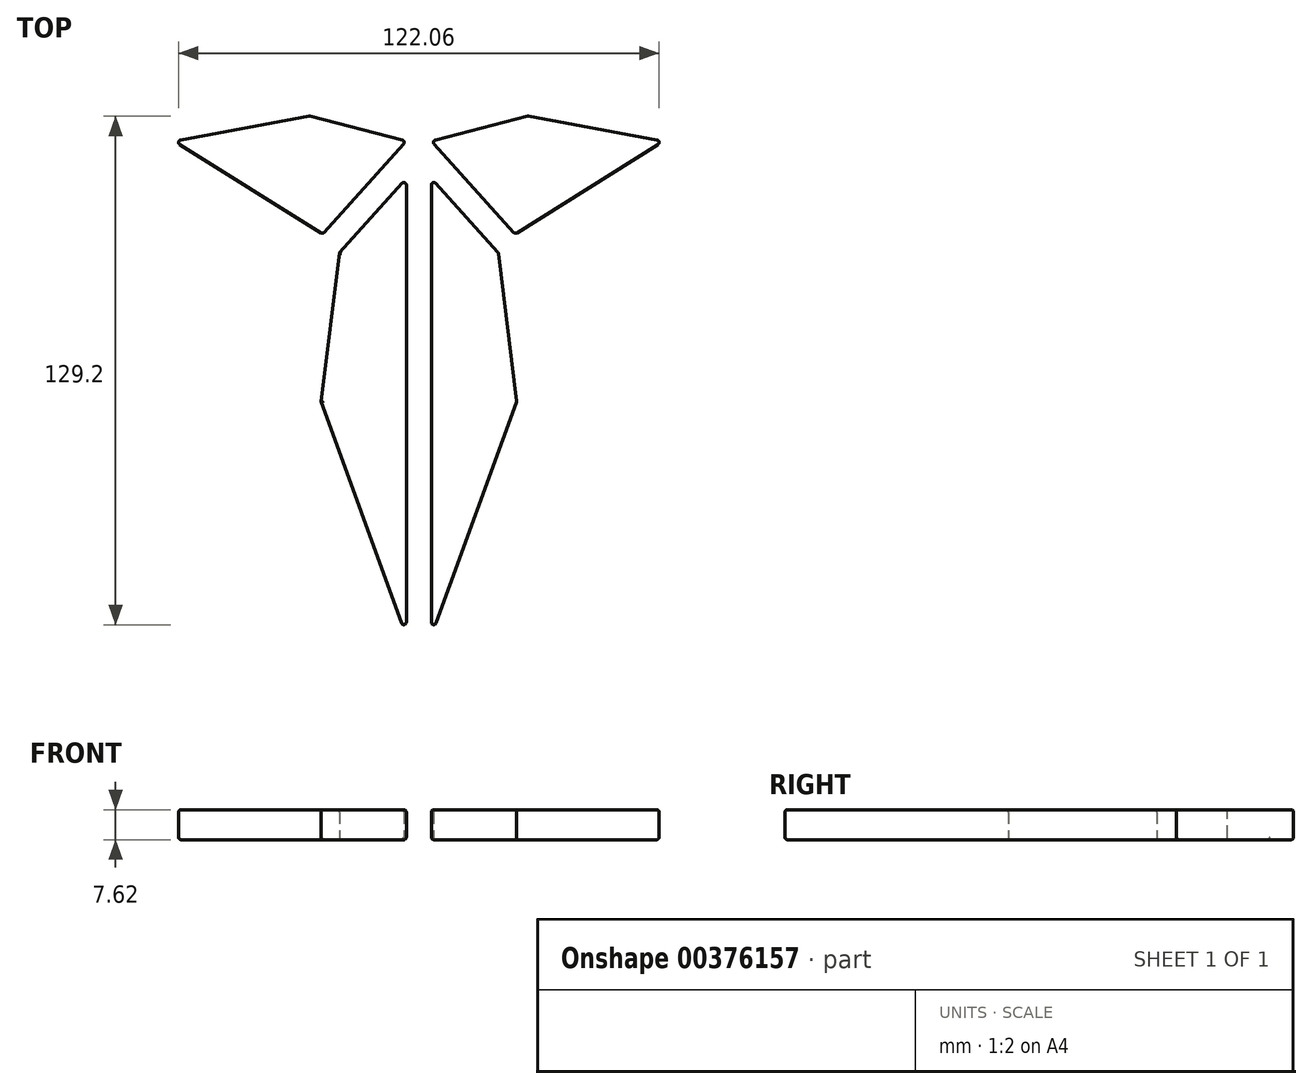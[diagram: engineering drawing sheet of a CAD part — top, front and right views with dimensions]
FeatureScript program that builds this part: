
annotation { "Feature Type Name" : "Feature", "Feature Type Description" : "" }
export const myFeature = defineFeature(function(context is Context, id is Id, definition is map)
    precondition{}
    {
        {
            var Q0;
            Q0=qCreatedBy(makeId("Top.planeOp"),FACE);
            var sketch = newSketch(context, id + "F0", { "sketchPlane" : qUnion([Q0])});
            skLineSegment(sketch, "E0", {"start": v(-3.18, 88.64) * mm, "end": v(-24.44, 65.06) * mm});
            skLineSegment(sketch, "E1", {"start": v(-24.44, 65.06) * mm, "end": v(-62.12, 88.64) * mm});
            skLineSegment(sketch, "E2", {"start": v(-62.12, 88.64) * mm, "end": v(-27.77, 94.98) * mm});
            skLineSegment(sketch, "E3", {"start": v(-27.77, 94.98) * mm, "end": v(-3.18, 88.64) * mm});
            skLineSegment(sketch, "E4", {"start": v(-3.18, 79.16) * mm, "end": v(-20.18, 60.3) * mm});
            skLineSegment(sketch, "E5", {"start": v(-20.18, 60.3) * mm, "end": v(-24.85, 22.48) * mm});
            skLineSegment(sketch, "E6", {"start": v(-3.18, 79.16) * mm, "end": v(-3.17, -37.2) * mm});
            skLineSegment(sketch, "E7", {"start": v(-3.17, -37.2) * mm, "end": v(-24.85, 22.48) * mm});
            skLineSegment(sketch, "E8.MirrorCS", {"start": v(27.77, 94.98) * mm, "end": v(3.18, 88.64) * mm});
            skLineSegment(sketch, "E9.MirrorCS", {"start": v(3.18, 79.16) * mm, "end": v(3.17, -37.2) * mm});
            skLineSegment(sketch, "E10.MirrorCS", {"start": v(24.44, 65.06) * mm, "end": v(62.12, 88.64) * mm});
            skLineSegment(sketch, "E11.MirrorCS", {"start": v(3.18, 88.64) * mm, "end": v(24.44, 65.06) * mm});
            skLineSegment(sketch, "E12.MirrorCS", {"start": v(3.18, 79.16) * mm, "end": v(20.18, 60.3) * mm});
            skLineSegment(sketch, "E13.MirrorCS", {"start": v(62.12, 88.64) * mm, "end": v(27.77, 94.98) * mm});
            skLineSegment(sketch, "E14.MirrorCS", {"start": v(3.17, -37.2) * mm, "end": v(24.85, 22.48) * mm});
            skLineSegment(sketch, "E15.MirrorCS", {"start": v(20.18, 60.3) * mm, "end": v(24.85, 22.48) * mm});
            skSolve(sketch);
        }
        {
            var Q0;
            Q0=makeQuery(id+"F0.imprint","IMPRINT",FACE,{"disambiguationData":[TD([[makeQuery(id+"F0.imprint","IMPRINT",EDGE,{"derivedFrom":sQuery(id+"F0.wireOp",EDGE,"E9.MirrorCS")}),1.0]])]});
            var Q1;
            Q1=makeQuery(id+"F0.imprint","IMPRINT",FACE,{"disambiguationData":[TD([[makeQuery(id+"F0.imprint","IMPRINT",EDGE,{"derivedFrom":sQuery(id+"F0.wireOp",EDGE,"E0")}),-1.0]])]});
            var Q2;
            Q2=makeQuery(id+"F0.imprint","IMPRINT",FACE,{"disambiguationData":[TD([[makeQuery(id+"F0.imprint","IMPRINT",EDGE,{"derivedFrom":sQuery(id+"F0.wireOp",EDGE,"E4")}),1.0]])]});
            var Q3;
            Q3=makeQuery(id+"F0.imprint","IMPRINT",FACE,{"disambiguationData":[TD([[makeQuery(id+"F0.imprint","IMPRINT",EDGE,{"derivedFrom":sQuery(id+"F0.wireOp",EDGE,"E8.MirrorCS")}),1.0]])]});
            extrude(context, id + "F1", {"entities" : qUnion([Q0, Q1, Q2, Q3]), "depth" : 7.62 * mm});
        }
        {
            var Q0;
            Q0=makeQuery(id+"F1.opExtrude","SWEPT_EDGE",EDGE,{"disambiguationData":[OSD([sQuery(id+"F0.wireOp",EDGE,"E9.MirrorCS"),sQuery(id+"F0.wireOp",EDGE,"E14.MirrorCS")])]});
            var Q1;
            Q1=makeQuery(id+"F1.opExtrude","SWEPT_EDGE",EDGE,{"disambiguationData":[OSD([sQuery(id+"F0.wireOp",EDGE,"E6"),sQuery(id+"F0.wireOp",EDGE,"E7")])]});
            var Q2;
            Q2=makeQuery(id+"F1.opExtrude","SWEPT_EDGE",EDGE,{"disambiguationData":[OSD([sQuery(id+"F0.wireOp",EDGE,"E12.MirrorCS"),sQuery(id+"F0.wireOp",EDGE,"E15.MirrorCS")])]});
            var Q3;
            Q3=makeQuery(id+"F1.opExtrude","SWEPT_EDGE",EDGE,{"disambiguationData":[OSD([sQuery(id+"F0.wireOp",EDGE,"E14.MirrorCS"),sQuery(id+"F0.wireOp",EDGE,"E15.MirrorCS")])]});
            var Q4;
            Q4=makeQuery(id+"F1.opExtrude","SWEPT_EDGE",EDGE,{"disambiguationData":[OSD([sQuery(id+"F0.wireOp",EDGE,"E4"),sQuery(id+"F0.wireOp",EDGE,"E6")])]});
            var Q5;
            Q5=makeQuery(id+"F1.opExtrude","CAP_EDGE",EDGE,{"disambiguationData":[OSD([sQuery(id+"F0.wireOp",EDGE,"E1")])],"isStart":false});
            var Q6;
            Q6=makeQuery(id+"F1.opExtrude","SWEPT_EDGE",EDGE,{"disambiguationData":[OSD([sQuery(id+"F0.wireOp",EDGE,"E1"),sQuery(id+"F0.wireOp",EDGE,"E2")])]});
            var Q7;
            Q7=makeQuery(id+"F1.opExtrude","CAP_EDGE",EDGE,{"disambiguationData":[OSD([sQuery(id+"F0.wireOp",EDGE,"E1")])],"isStart":true});
            var Q8;
            Q8=makeQuery(id+"F1.opExtrude","CAP_EDGE",EDGE,{"disambiguationData":[OSD([sQuery(id+"F0.wireOp",EDGE,"E2")])],"isStart":false});
            var Q9;
            Q9=makeQuery(id+"F1.opExtrude","CAP_EDGE",EDGE,{"disambiguationData":[OSD([sQuery(id+"F0.wireOp",EDGE,"E3")])],"isStart":false});
            var Q10;
            Q10=makeQuery(id+"F1.opExtrude","CAP_EDGE",EDGE,{"disambiguationData":[OSD([sQuery(id+"F0.wireOp",EDGE,"E0")])],"isStart":false});
            var Q11;
            Q11=makeQuery(id+"F1.opExtrude","SWEPT_EDGE",EDGE,{"disambiguationData":[OSD([sQuery(id+"F0.wireOp",EDGE,"E0"),sQuery(id+"F0.wireOp",EDGE,"E3")])]});
            var Q12;
            Q12=makeQuery(id+"F1.opExtrude","SWEPT_EDGE",EDGE,{"disambiguationData":[OSD([sQuery(id+"F0.wireOp",EDGE,"E2"),sQuery(id+"F0.wireOp",EDGE,"E3")])]});
            var Q13;
            Q13=makeQuery(id+"F1.opExtrude","CAP_EDGE",EDGE,{"disambiguationData":[OSD([sQuery(id+"F0.wireOp",EDGE,"E3")])],"isStart":true});
            var Q14;
            Q14=makeQuery(id+"F1.opExtrude","CAP_EDGE",EDGE,{"disambiguationData":[OSD([sQuery(id+"F0.wireOp",EDGE,"E2")])],"isStart":true});
            var Q15;
            Q15=makeQuery(id+"F1.opExtrude","CAP_EDGE",EDGE,{"disambiguationData":[OSD([sQuery(id+"F0.wireOp",EDGE,"E11.MirrorCS")])],"isStart":false});
            var Q16;
            Q16=makeQuery(id+"F1.opExtrude","CAP_EDGE",EDGE,{"disambiguationData":[OSD([sQuery(id+"F0.wireOp",EDGE,"E12.MirrorCS")])],"isStart":false});
            var Q17;
            Q17=makeQuery(id+"F1.opExtrude","SWEPT_EDGE",EDGE,{"disambiguationData":[OSD([sQuery(id+"F0.wireOp",EDGE,"E9.MirrorCS"),sQuery(id+"F0.wireOp",EDGE,"E12.MirrorCS")])]});
            var Q18;
            Q18=makeQuery(id+"F1.opExtrude","CAP_EDGE",EDGE,{"disambiguationData":[OSD([sQuery(id+"F0.wireOp",EDGE,"E6")])],"isStart":false});
            var Q19;
            Q19=makeQuery(id+"F1.opExtrude","CAP_EDGE",EDGE,{"disambiguationData":[OSD([sQuery(id+"F0.wireOp",EDGE,"E4")])],"isStart":false});
            var Q20;
            Q20=makeQuery(id+"F1.opExtrude","CAP_EDGE",EDGE,{"disambiguationData":[OSD([sQuery(id+"F0.wireOp",EDGE,"E5")])],"isStart":false});
            var Q21;
            Q21=makeQuery(id+"F1.opExtrude","CAP_EDGE",EDGE,{"disambiguationData":[OSD([sQuery(id+"F0.wireOp",EDGE,"E7")])],"isStart":false});
            var Q22;
            Q22=makeQuery(id+"F1.opExtrude","CAP_EDGE",EDGE,{"disambiguationData":[OSD([sQuery(id+"F0.wireOp",EDGE,"E9.MirrorCS")])],"isStart":false});
            var Q23;
            Q23=makeQuery(id+"F1.opExtrude","CAP_EDGE",EDGE,{"disambiguationData":[OSD([sQuery(id+"F0.wireOp",EDGE,"E14.MirrorCS")])],"isStart":false});
            var Q24;
            Q24=makeQuery(id+"F1.opExtrude","SWEPT_FACE",FACE,{"disambiguationData":[OSD([sQuery(id+"F0.wireOp",EDGE,"E15.MirrorCS")])]});
            var Q25;
            Q25=makeQuery(id+"F1.opExtrude","SWEPT_FACE",FACE,{"disambiguationData":[OSD([sQuery(id+"F0.wireOp",EDGE,"E14.MirrorCS")])]});
            var Q26;
            Q26=makeQuery(id+"F1.opExtrude","CAP_FACE",FACE,{"disambiguationData":[OSD([sQuery(id+"F0.wireOp",EDGE,"E8.MirrorCS"),sQuery(id+"F0.wireOp",EDGE,"E10.MirrorCS"),sQuery(id+"F0.wireOp",EDGE,"E11.MirrorCS"),sQuery(id+"F0.wireOp",EDGE,"E13.MirrorCS")])],"isStart":false});
            var Q27;
            Q27=makeQuery(id+"F1.opExtrude","CAP_EDGE",EDGE,{"disambiguationData":[OSD([sQuery(id+"F0.wireOp",EDGE,"E13.MirrorCS")])],"isStart":false});
            var Q28;
            Q28=makeQuery(id+"F1.opExtrude","CAP_EDGE",EDGE,{"disambiguationData":[OSD([sQuery(id+"F0.wireOp",EDGE,"E8.MirrorCS")])],"isStart":true});
            var Q29;
            Q29=makeQuery(id+"F1.opExtrude","SWEPT_FACE",FACE,{"disambiguationData":[OSD([sQuery(id+"F0.wireOp",EDGE,"E13.MirrorCS")])]});
            var Q30;
            Q30=makeQuery(id+"F1.opExtrude","CAP_EDGE",EDGE,{"disambiguationData":[OSD([sQuery(id+"F0.wireOp",EDGE,"E10.MirrorCS")])],"isStart":false});
            var Q31;
            Q31=makeQuery(id+"F1.opExtrude","SWEPT_FACE",FACE,{"disambiguationData":[OSD([sQuery(id+"F0.wireOp",EDGE,"E10.MirrorCS")])]});
            var Q32;
            Q32=makeQuery(id+"F1.opExtrude","CAP_EDGE",EDGE,{"disambiguationData":[OSD([sQuery(id+"F0.wireOp",EDGE,"E11.MirrorCS")])],"isStart":true});
            var Q33;
            Q33=makeQuery(id+"F1.opExtrude","SWEPT_EDGE",EDGE,{"disambiguationData":[OSD([sQuery(id+"F0.wireOp",EDGE,"E8.MirrorCS"),sQuery(id+"F0.wireOp",EDGE,"E11.MirrorCS")])]});
            var Q34;
            Q34=makeQuery(id+"F1.opExtrude","SWEPT_EDGE",EDGE,{"disambiguationData":[OSD([sQuery(id+"F0.wireOp",EDGE,"E0"),sQuery(id+"F0.wireOp",EDGE,"E1")])]});
            var Q35;
            Q35=makeQuery(id+"F1.opExtrude","CAP_FACE",FACE,{"disambiguationData":[OSD([sQuery(id+"F0.wireOp",EDGE,"E4"),sQuery(id+"F0.wireOp",EDGE,"E5"),sQuery(id+"F0.wireOp",EDGE,"E6"),sQuery(id+"F0.wireOp",EDGE,"E7")])],"isStart":true});
            var Q36;
            Q36=makeQuery(id+"F1.opExtrude","CAP_FACE",FACE,{"disambiguationData":[OSD([sQuery(id+"F0.wireOp",EDGE,"E9.MirrorCS"),sQuery(id+"F0.wireOp",EDGE,"E12.MirrorCS"),sQuery(id+"F0.wireOp",EDGE,"E14.MirrorCS"),sQuery(id+"F0.wireOp",EDGE,"E15.MirrorCS")])],"isStart":true});
            fillet(context, id + "F2", {"entities" : qUnion([Q0, Q1, Q2, Q3, Q4, Q5, Q6, Q7, Q8, Q9, Q10, Q11, Q12, Q13, Q14, Q15, Q16, Q17, Q18, Q19, Q20, Q21, Q22, Q23, Q24, Q25, Q26, Q27, Q28, Q29, Q30, Q31, Q32, Q33, Q34, Q35, Q36]), "radius" : 0.64 * mm, "tangentPropagation" : true, "allowEdgeOverflow" : false});
        }
    });
